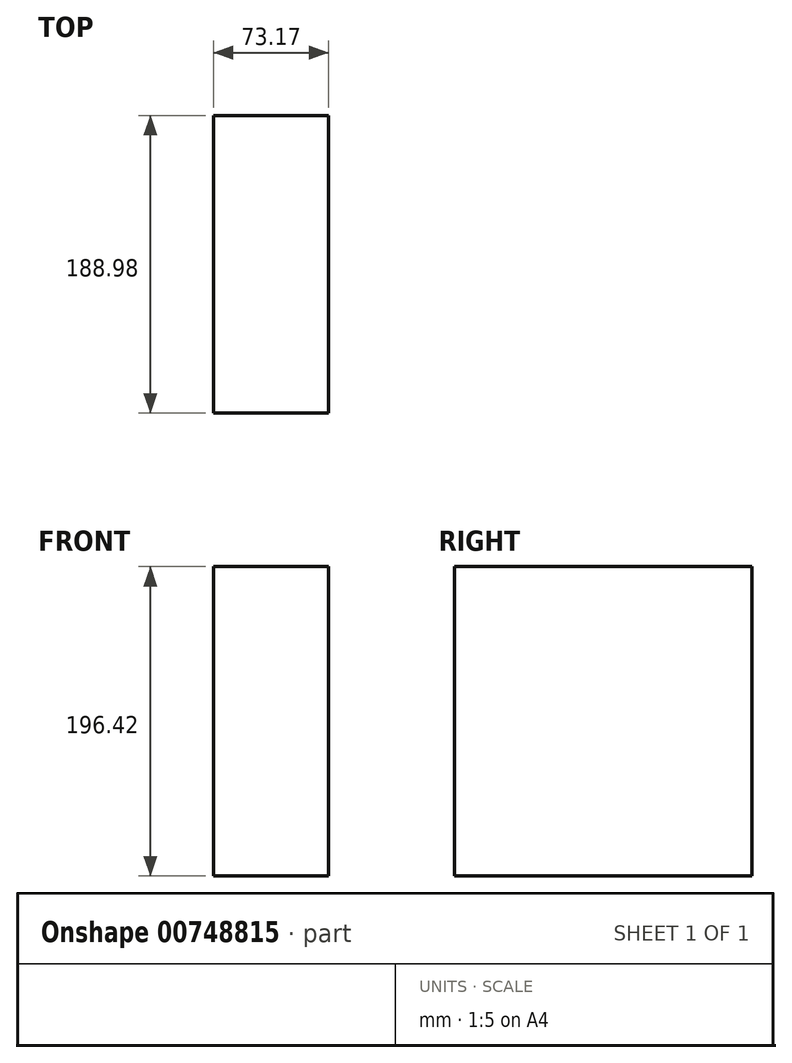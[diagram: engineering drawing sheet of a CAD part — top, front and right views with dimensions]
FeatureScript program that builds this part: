
annotation { "Feature Type Name" : "Feature", "Feature Type Description" : "" }
export const myFeature = defineFeature(function(context is Context, id is Id, definition is map)
    precondition{}
    {
        {
            var Q0;
            Q0=qCreatedBy(makeId("Top.planeOp"),FACE);
            var sketch = newSketch(context, id + "F0", { "sketchPlane" : qUnion([Q0])});
            skLineSegment(sketch, "E0.bottom", {"start": v(37.69, 63.53) * mm, "end": v(-37.69, 63.53) * mm});
            skLineSegment(sketch, "E0.top", {"start": v(37.69, -9.33) * mm, "end": v(-37.69, -9.33) * mm});
            skLineSegment(sketch, "E0.left", {"start": v(37.69, 63.53) * mm, "end": v(37.69, -9.33) * mm});
            skLineSegment(sketch, "E0.right", {"start": v(-37.69, 63.53) * mm, "end": v(-37.69, -9.33) * mm});
            skPoint(sketch, "E0.middle", {"position": v(0, 27.1) * mm});
            skLineSegment(sketch, "E1.bottom", {"start": v(0, 27.1) * mm, "end": v(0, 27.1) * mm});
            skLineSegment(sketch, "E1.top", {"start": v(0, 27.1) * mm, "end": v(0, 27.1) * mm});
            skLineSegment(sketch, "E1.left", {"start": v(0, 27.1) * mm, "end": v(0, 27.1) * mm});
            skLineSegment(sketch, "E1.right", {"start": v(0, 27.1) * mm, "end": v(0, 27.1) * mm});
            skLineSegment(sketch, "E2.bottom", {"start": v(-35.48, -276.47) * mm, "end": v(51.53, -276.47) * mm});
            skLineSegment(sketch, "E2.top", {"start": v(-35.48, 265.52) * mm, "end": v(51.53, 265.52) * mm});
            skLineSegment(sketch, "E2.left", {"start": v(-35.48, -276.47) * mm, "end": v(-35.48, 265.52) * mm});
            skLineSegment(sketch, "E2.right", {"start": v(51.53, -276.47) * mm, "end": v(51.53, 265.52) * mm});
            skPoint(sketch, "E2.middle", {"position": v(8.03, -5.48) * mm});
            skSolve(sketch);
        }
        {
            var Q0;
            {var subQ0=sQuery(id+"F0.wireOp",EDGE,"E0.left");Q0=makeQuery(id+"F0.imprint","IMPRINT",FACE,{"disambiguationData":[TD([[makeQuery(id+"F0.imprint","IMPRINT",EDGE,{"derivedFrom":subQ0}),-1.0]])]});}
            extrude(context, id + "F1", {"entities" : qUnion([Q0]), "depth" : 196.42 * mm, "offsetDistance" : 25.4 * mm});
        }
        {
            var Q0;
            Q0=makeQuery(id+"F1.opExtrude","SWEPT_FACE",FACE,{"disambiguationData":[OSD([sQuery(id+"F0.wireOp",EDGE,"E0.top")])]});
            extrude(context, id + "F2", {"entities" : qUnion([Q0]), "operationType" : NewBodyOperationType.ADD, "depth" : 116.13 * mm, "offsetDistance" : 25.4 * mm});
        }
        {
            var Q0;
            {var subQ0=sQuery(id+"F0.wireOp",EDGE,"E0.top");Q0=makeQuery(id+"F2.boolean.opBoolean","MERGE",FACE,{"derivedFrom":[makeQuery(id+"F1.opExtrude","CAP_FACE",FACE,{"disambiguationData":[OSD([sQuery(id+"F0.wireOp",EDGE,"E0.bottom"),subQ0,sQuery(id+"F0.wireOp",EDGE,"E0.left"),sQuery(id+"F0.wireOp",EDGE,"E2.left")])],"isStart":false}),makeQuery(id+"F2.opExtrude","SWEPT_FACE",FACE,{"disambiguationData":[OSD([subQ0]),TDD([makeQuery(id+"F1.opExtrude","CAP_EDGE",EDGE,{"disambiguationData":[OSD([subQ0])],"isStart":false})])]})]});}
            var sketch = newSketch(context, id + "F3", { "sketchPlane" : qUnion([Q0])});
            skLineSegment(sketch, "E3.bottom", {"start": v(0, 0) * mm, "end": v(-35.48, 0) * mm});
            skLineSegment(sketch, "E3.top", {"start": v(0, 25.55) * mm, "end": v(-35.48, 25.55) * mm});
            skLineSegment(sketch, "E3.left", {"start": v(0, 0) * mm, "end": v(0, 25.55) * mm});
            skLineSegment(sketch, "E3.right", {"start": v(-35.48, 0) * mm, "end": v(-35.48, 25.55) * mm});
            skSolve(sketch);
        }
        {
            var Q0;
            Q0 = qSketchRegion(id + "F3", true);
            var Q1;
            {var subQ2=sQuery(id+"F3.wireOp",EDGE,"E3.bottom");Q1=makeQuery(id+"F3.imprint","IMPRINT",FACE,{"disambiguationData":[TD([[makeQuery(id+"F3.imprint","IMPRINT",EDGE,{"derivedFrom":subQ2}),1.0]])]});}
            extrude(context, id + "F4", {"entities" : qUnion([Q0, Q1]), "operationType" : NewBodyOperationType.ADD, "oppositeDirection" : true, "depth" : 137.58 * mm, "offsetDistance" : 25.4 * mm});
        }
    });
